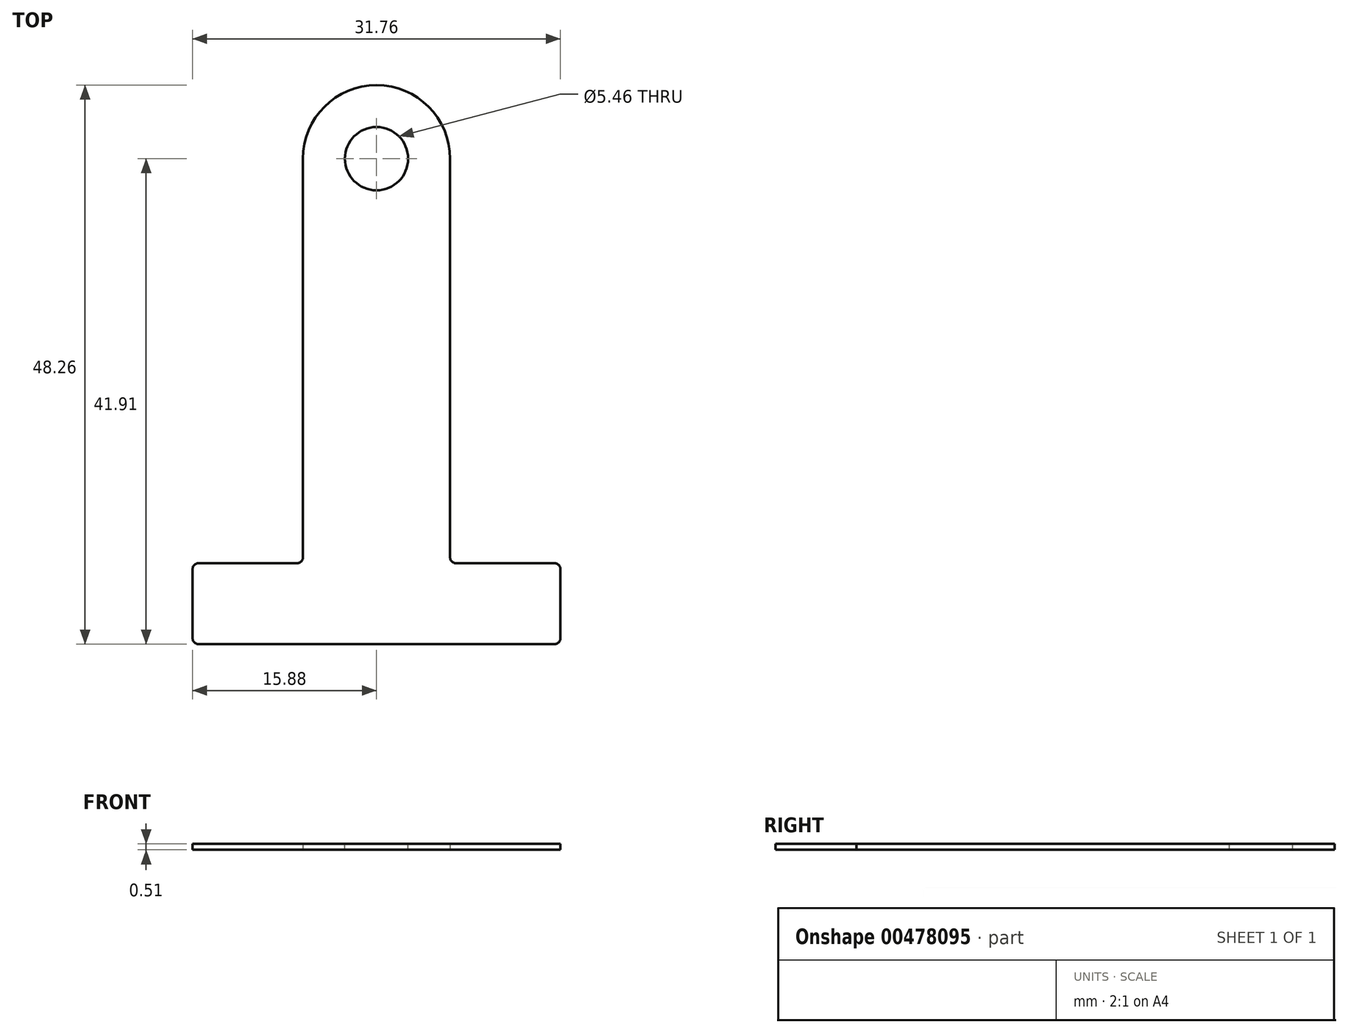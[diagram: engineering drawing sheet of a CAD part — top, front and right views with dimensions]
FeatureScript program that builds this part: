
annotation { "Feature Type Name" : "Feature", "Feature Type Description" : "" }
export const myFeature = defineFeature(function(context is Context, id is Id, definition is map)
    precondition{}
    {
        {
            var Q0;
            Q0=qCreatedBy(makeId("Top.planeOp"),FACE);
            var sketch = newSketch(context, id + "F0", { "sketchPlane" : qUnion([Q0])});
            skLineSegment(sketch, "E0", {"start": v(0, 0) * mm, "end": v(-15.87, 0) * mm});
            skLineSegment(sketch, "E1", {"start": v(-15.87, 0) * mm, "end": v(-15.87, 6.99) * mm});
            skLineSegment(sketch, "E2", {"start": v(-15.87, 6.99) * mm, "end": v(-6.35, 6.99) * mm});
            skLineSegment(sketch, "E3", {"start": v(-6.35, 6.99) * mm, "end": v(-6.35, 41.91) * mm});
            skArc(sketch, "E4", {"start": v(-6.35, 41.91) * mm, "mid": v(-4.5, 46.4) * mm, "end": v(0, 48.26) * mm});
            skLineSegment(sketch, "E5", {"start": v(0, 52.6) * mm, "end": v(0, 21.74) * mm, "construction": true});
            skLineSegment(sketch, "E6.MirrorCS", {"start": v(0, 0) * mm, "end": v(15.88, 0) * mm});
            skLineSegment(sketch, "E7.MirrorCS", {"start": v(15.88, 0) * mm, "end": v(15.88, 6.99) * mm});
            skLineSegment(sketch, "E8.MirrorCS", {"start": v(6.35, 6.99) * mm, "end": v(6.35, 41.91) * mm});
            skLineSegment(sketch, "E9.MirrorCS", {"start": v(15.88, 6.99) * mm, "end": v(6.35, 6.99) * mm});
            skArc(sketch, "E10.MirrorCS", {"start": v(6.35, 41.91) * mm, "mid": v(4.5, 46.4) * mm, "end": v(0, 48.26) * mm});
            skSolve(sketch);
        }
        {
            var Q0;
            Q0=makeQuery(id+"F0.imprint","IMPRINT",FACE,{"disambiguationData":[TD([[makeQuery(id+"F0.imprint","IMPRINT",EDGE,{"derivedFrom":sQuery(id+"F0.wireOp",EDGE,"E0")}),-1.0]])]});
            extrude(context, id + "F1", {"entities" : qUnion([Q0]), "depth" : 0.5 * mm});
        }
        {
            var Q0;
            Q0=makeQuery(id+"F1.opExtrude","CAP_FACE",FACE,{"disambiguationData":[OSD([sQuery(id+"F0.wireOp",EDGE,"E0"),sQuery(id+"F0.wireOp",EDGE,"E1"),sQuery(id+"F0.wireOp",EDGE,"E2"),sQuery(id+"F0.wireOp",EDGE,"E3"),sQuery(id+"F0.wireOp",EDGE,"E4"),sQuery(id+"F0.wireOp",EDGE,"E6.MirrorCS"),sQuery(id+"F0.wireOp",EDGE,"E7.MirrorCS"),sQuery(id+"F0.wireOp",EDGE,"E8.MirrorCS"),sQuery(id+"F0.wireOp",EDGE,"E9.MirrorCS"),sQuery(id+"F0.wireOp",EDGE,"E10.MirrorCS")])],"isStart":false});
            var sketch = newSketch(context, id + "F2", { "sketchPlane" : qUnion([Q0])});
            skCircle(sketch, "E11", {"center": v(0, 41.91) * mm, "radius": 2.73 * mm});
            skSolve(sketch);
        }
        {
            var Q0;
            Q0 = qSketchRegion(id + "F2", true);
            extrude(context, id + "F3", {"entities" : qUnion([Q0]), "operationType" : NewBodyOperationType.REMOVE, "endBound" : BoundingType.THROUGH_ALL, "oppositeDirection" : true, "depth" : 25.4 * mm});
        }
        {
            var Q0;
            Q0=makeQuery(id+"F1.opExtrude","SWEPT_EDGE",EDGE,{"disambiguationData":[OSD([sQuery(id+"F0.wireOp",EDGE,"E0"),sQuery(id+"F0.wireOp",EDGE,"E1")])]});
            var Q1;
            Q1=makeQuery(id+"F1.opExtrude","SWEPT_EDGE",EDGE,{"disambiguationData":[OSD([sQuery(id+"F0.wireOp",EDGE,"E1"),sQuery(id+"F0.wireOp",EDGE,"E2")])]});
            var Q2;
            Q2=makeQuery(id+"F1.opExtrude","SWEPT_EDGE",EDGE,{"disambiguationData":[OSD([sQuery(id+"F0.wireOp",EDGE,"E7.MirrorCS"),sQuery(id+"F0.wireOp",EDGE,"E9.MirrorCS")])]});
            var Q3;
            Q3=makeQuery(id+"F1.opExtrude","SWEPT_EDGE",EDGE,{"disambiguationData":[OSD([sQuery(id+"F0.wireOp",EDGE,"E6.MirrorCS"),sQuery(id+"F0.wireOp",EDGE,"E7.MirrorCS")])]});
            var Q4;
            Q4=makeQuery(id+"F1.opExtrude","SWEPT_EDGE",EDGE,{"disambiguationData":[OSD([sQuery(id+"F0.wireOp",EDGE,"E8.MirrorCS"),sQuery(id+"F0.wireOp",EDGE,"E9.MirrorCS")])]});
            var Q5;
            Q5=makeQuery(id+"F1.opExtrude","SWEPT_EDGE",EDGE,{"disambiguationData":[OSD([sQuery(id+"F0.wireOp",EDGE,"E2"),sQuery(id+"F0.wireOp",EDGE,"E3")])]});
            fillet(context, id + "F4", {"entities" : qUnion([Q0, Q1, Q2, Q3, Q4, Q5]), "radius" : 0.5 * mm, "tangentPropagation" : true, "allowEdgeOverflow" : false});
        }
    });
